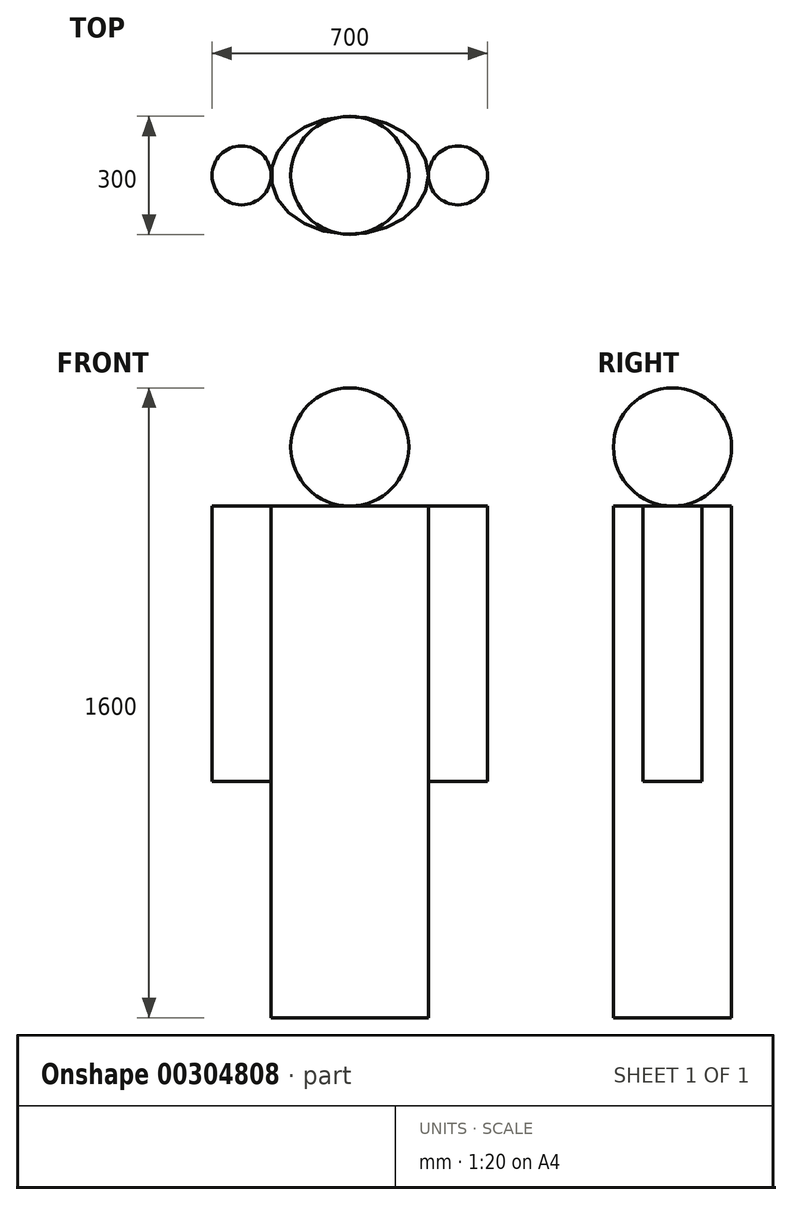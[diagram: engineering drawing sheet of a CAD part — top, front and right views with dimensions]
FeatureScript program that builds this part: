
annotation { "Feature Type Name" : "Feature", "Feature Type Description" : "" }
export const myFeature = defineFeature(function(context is Context, id is Id, definition is map)
    precondition{}
    {
        {
            var Q0;
            Q0=qCreatedBy(makeId("Top.planeOp"),FACE);
            var sketch = newSketch(context, id + "F0", { "sketchPlane" : qUnion([Q0])});
            skCircle(sketch, "E0", {"center": v(275, 0) * mm, "radius": 75 * mm});
            skCircle(sketch, "E1", {"center": v(-275, 0) * mm, "radius": 75 * mm});
            skEllipse(sketch, "E2", {"center": v(0, 0) * mm, "majorRadius": 200 * mm, "minorRadius": 150 * mm, "majorAxis": v(1, 0)});
            skSolve(sketch);
        }
        {
            var Q0;
            Q0=qCreatedBy(makeId("Front.planeOp"),FACE);
            var sketch = newSketch(context, id + "F1", { "sketchPlane" : qUnion([Q0])});
            skArc(sketch, "E3", {"start": v(0, 700) * mm, "mid": v(150, 850) * mm, "end": v(0, 1000) * mm});
            skLineSegment(sketch, "E4", {"start": v(0, 1000) * mm, "end": v(0, 700) * mm});
            skSolve(sketch);
        }
        {
            var Q0;
            Q0=makeQuery(id+"F1.imprint","IMPRINT",FACE,{"disambiguationData":[TD([[makeQuery(id+"F1.imprint","IMPRINT",EDGE,{"derivedFrom":sQuery(id+"F1.wireOp",EDGE,"E3")}),1.0]])]});
            var Q1;
            Q1=sQuery(id+"F1.wireOp",EDGE,"E4");
            revolve(context, id + "F2", {"entities" : qUnion([Q0]), "axis" : qUnion([Q1]), "revolveType" : RevolveType.FULL});
        }
        {
            var Q0;
            Q0 = qSketchRegion(id + "F0", true);
            extrude(context, id + "F3", {"entities" : qUnion([Q0]), "depth" : 700 * mm});
        }
        {
            var Q0;
            Q0=makeQuery(id+"F3.opExtrude","CAP_FACE",FACE,{"disambiguationData":[OSD([sQuery(id+"F0.wireOp",EDGE,"E2")])],"isStart":true});
            extrude(context, id + "F4", {"entities" : qUnion([Q0]), "operationType" : NewBodyOperationType.ADD, "depth" : 600 * mm});
        }
    });
